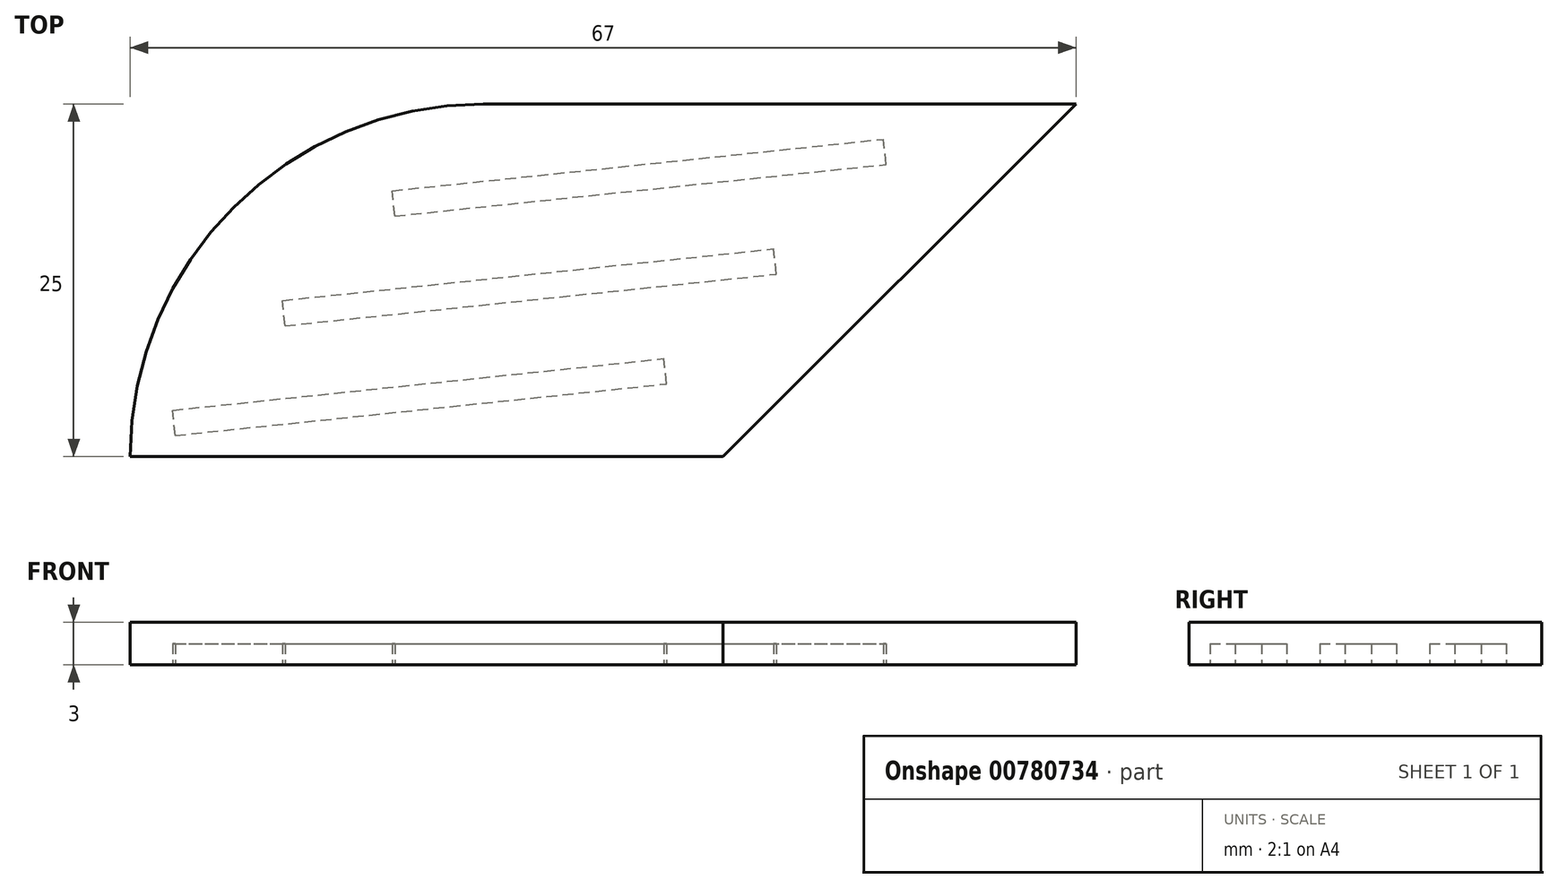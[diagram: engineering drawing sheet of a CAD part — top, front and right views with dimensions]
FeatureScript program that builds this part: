
annotation { "Feature Type Name" : "Feature", "Feature Type Description" : "" }
export const myFeature = defineFeature(function(context is Context, id is Id, definition is map)
    precondition{}
    {
        {
            var Q0;
            Q0=qCreatedBy(makeId("Top.planeOp"),FACE);
            var sketch = newSketch(context, id + "F0", { "sketchPlane" : qUnion([Q0])});
            skLineSegment(sketch, "E0.bottom", {"start": v(0, 0) * mm, "end": v(42, 0) * mm});
            skLineSegment(sketch, "E0.top", {"start": v(25, 25) * mm, "end": v(42, 25) * mm});
            skLineSegment(sketch, "E0.left", {"start": v(0, 0) * mm, "end": v(0, 0) * mm});
            skLineSegment(sketch, "E0.right", {"start": v(42, 0) * mm, "end": v(42, 25) * mm});
            skPoint(sketch, "E1.visualSharp", {"position": v(0, 25) * mm});
            skArc(sketch, "E1.filletArc", {"start": v(25, 25) * mm, "mid": v(7.32, 17.68) * mm, "end": v(0, 0) * mm});
            skLineSegment(sketch, "E2", {"start": v(42, 25) * mm, "end": v(67, 25) * mm});
            skLineSegment(sketch, "E3", {"start": v(67, 25) * mm, "end": v(42, 0) * mm});
            skSolve(sketch);
        }
        {
            var Q0;
            Q0=qSketchRegion(id+"F0",true);
            extrude(context, id + "F1", {"entities" : qUnion([Q0]), "depth" : 3 * mm, "offsetDistance" : 25 * mm});
        }
        {
            var Q0;
            Q0=qCreatedBy(makeId("Top.planeOp"),FACE);
            var sketch = newSketch(context, id + "F2", { "sketchPlane" : qUnion([Q0])});
            skLineSegment(sketch, "E4.bottom", {"start": v(3.2, 1.5) * mm, "end": v(38, 5.16) * mm});
            skLineSegment(sketch, "E4.top", {"start": v(3, 3.3) * mm, "end": v(37.81, 6.95) * mm});
            skLineSegment(sketch, "E4.left", {"start": v(3.2, 1.5) * mm, "end": v(3, 3.3) * mm});
            skLineSegment(sketch, "E4.right", {"start": v(38, 5.16) * mm, "end": v(37.81, 6.95) * mm});
            skLineSegment(sketch, "E5.0.1.0", {"start": v(10.97, 9.28) * mm, "end": v(10.78, 11.07) * mm});
            skLineSegment(sketch, "E5.0.1.1", {"start": v(10.78, 11.07) * mm, "end": v(45.6, 14.73) * mm});
            skLineSegment(sketch, "E5.0.1.2", {"start": v(10.97, 9.28) * mm, "end": v(45.78, 12.94) * mm});
            skLineSegment(sketch, "E5.0.1.3", {"start": v(45.78, 12.94) * mm, "end": v(45.6, 14.73) * mm});
            skLineSegment(sketch, "E5.0.2.0", {"start": v(18.75, 17.06) * mm, "end": v(18.56, 18.85) * mm});
            skLineSegment(sketch, "E5.0.2.1", {"start": v(18.56, 18.85) * mm, "end": v(53.37, 22.5) * mm});
            skLineSegment(sketch, "E5.0.2.2", {"start": v(18.75, 17.06) * mm, "end": v(53.56, 20.71) * mm});
            skLineSegment(sketch, "E5.0.2.3", {"start": v(53.56, 20.71) * mm, "end": v(53.37, 22.5) * mm});
            skLineSegment(sketch, "E5.direction1", {"start": v(3.2, 1.5) * mm, "end": v(38.14, 1.5) * mm, "construction": true});
            skLineSegment(sketch, "E5.direction2", {"start": v(3.2, 1.5) * mm, "end": v(10.97, 9.28) * mm, "construction": true});
            skSolve(sketch);
        }
        {
            var Q0;
            Q0=qSketchRegion(id+"F2",true);
            extrude(context, id + "F3", {"entities" : qUnion([Q0]), "operationType" : NewBodyOperationType.REMOVE, "depth" : 1.5 * mm, "offsetDistance" : 25 * mm});
        }
    });
